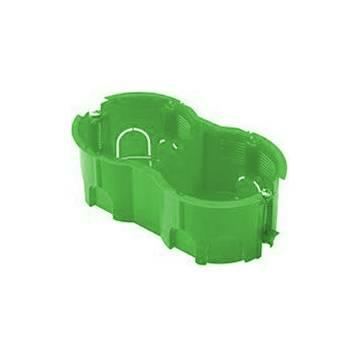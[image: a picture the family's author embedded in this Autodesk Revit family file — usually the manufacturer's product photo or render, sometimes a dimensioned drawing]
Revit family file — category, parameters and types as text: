
# Revit family: Building-ContenitoriIncasso-GEWISS-24SC-GREENWALL-SCATOLE-INCASSO_TONDE_DOPPIE
name_source: partatom
category: Apparecchi elettrici
revit_build: Autodesk Revit 2016 (Build: 20161004_0715(x64)
units: mm (PartAtom-declared; Revit-internal decimal feet)

## family parameters
Condiviso = Sì
Host = Superficie
Mantenere orientamento annotazione = Sì
Numero OmniClass = 23.80.30.14.24
Punto di calcolo locali = Sì
Quota connettore circolare = Usa diametro
Taglio con vuoti quando caricato = Sì
Tipo di parte = Normale
Titolo OmniClass = Junction Boxes

## types (1)
- GW24282PM - Halogen free - 125x72x45
    Caratteristiche = Halogen free
    Carico apparente = 0 VA
    Catalogo = BUILDING
    Catalogo Serie = 24SC
    Classificazione = Altro
    Codice EAN = 8011564802032
    Codice Electrocod = 0210
    Descrizione = SCATOLA 2+2 POSTI PARETI LEGGERE GREEN
    Descrizione: = Doppia
    Dimensioni (mm) = 125x72x45
    Glow Wire Test = 850°C
    Grado di protezione = IP40
    IDF = 39e1a116-dd26-474e-b298-5156098be0e7
    IDT = 5e032acf-9e89-4430-9960-546520e20b75
    Immagine tipo = GW24282PM.jpg
    Installazione = Incasso
    Interasse placche Chorus International = 57MM
    Metallo = GEWISS - Elementi acciaio
    Modello = GW24282PM
    Per Pareti = Cartongesso
    Produttore = GEWISS S.p.A.
    Profondità = 45 mm  [stored 0.147638 ft]
    Prospetto di default = 1219.2 mm
    Resistenza agli urti = IK07
    SEO = Scatola
    Scatola = GEWISS - scatola a incasso
    Scheda Tecnica = https://www.gewiss.com
    Temperatura di impiego = -15 +60 °C
    Termopressione con biglia = 70 °C
    Tipo Materiale = Halogen free secondo norma EN 60754-2
    URL = https://www.gewiss.com
    Versione file RFA = 19.0
    Voltaggio = 0 V

note: [stored X ft] marks values corroborated as IEEE doubles in the binary element streams (Revit-internal decimal feet)

## geometry (parser evidence)
native form markers: Sweep x2
no freeform markers — native parametric forms only
